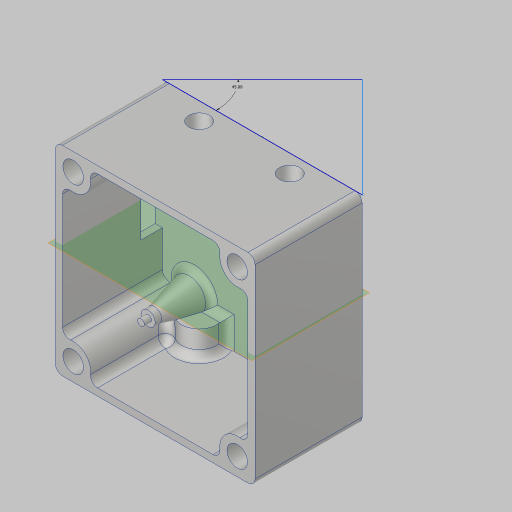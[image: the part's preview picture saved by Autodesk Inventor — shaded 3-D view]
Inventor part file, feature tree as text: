
AUTODESK INVENTOR PART (.ipt)
format: ipt  version: 2023.5 (Build 275446000, 446)  size: 542,720 bytes
history: native  units: in
note: dims shown in document units (in); Inventor stores cm internally (conversion verified against a paired STEP export)
features: extrude x6, projected_geometry x4, fillet x2, chamfer x2, sketch x2, hole x1, mirror x1, shell x1, plane x1
ambient origin geometry x8: Origin, YZ Plane, XZ Plane, XY Plane, X Axis, Y Axis, Z Axis, Center Point
bodies: Solid1 (feature_tree)
feature tree (20):
  extrude  "Extrusion1"  Depth=1.4961in
  hole  "Hole1"  [1 undecoded]
  extrude  "Extrusion6"  Depth=0.0787in TaperAngle=0.0deg
  mirror  "Mirror1"
  shell  "Shell1"  Thickness=0.0787in
  fillet  "Fillet1"  Radius=0.3937in
  extrude  "Extrusion2"  Depth=0.0787in
  chamfer  "Chamfer1"  Distance=0.0787in
  extrude  "Extrusion3"  Depth=0.0787in
  extrude  "Extrusion4"  Depth=0.0787in
  plane  "Work Plane1"
  extrude  "Extrusion5"  Depth=0.0787in
  chamfer  "Chamfer2"  Distance=0.1575in
  fillet  "Fillet3"  Radius=0.5906in
  sketch  "Sketch8"  dims[d2=1.3386in d3=1.3386in d5=1.1811in d6=0.0in d7=0.0787in d8=0.3937in d9=1.811in d10=0.2283in d11=0.2362in d12=0.385in d13=0.0787in d14=0.5635in d15=0.315in d16=0.8108in d17=0.0787in d18=0.1575in d19=0.1575in d20=0.1575in d21=0.1575in d22=0.5906in d23=0.0in d24=0.1181in d25=0.0787in d26=75.0deg d27=0.0748in d28=0.0748in d29=0.0748in d30=0.0748in d31=0.0787in d32=0.0in d33=0.4724in d34=0.2362in d35=0.0787in d36=1.1811in d37=0.0in d38=-1.25in d39=45.0deg d40=0.1969in d41=0.0787in d42=0.1969in d43=0.0in d44=0.0197in d45=0.0787in d46=0.481in d47=0.2283in d48=0.2283in d49=0.1969in d50=1.0in d51=0.2756in d52=0.0in d61=0.0787in d62=45.0deg d60=0.0in d63=0.0in]
  projected_geometry  "Projected Loop1"
  projected_geometry  "Projected Loop2"
  projected_geometry  "Projected Loop3"
  sketch  "Sketch5"  dims[d0=1.4961in d1=1.4961in]
  projected_geometry  "Project Cut Edges1"
note: 1 required parameter value undecoded (feature->parameter linkage not recoverable at this tier; creation-order binding heuristic only, values carry confidence <= 0.55)
